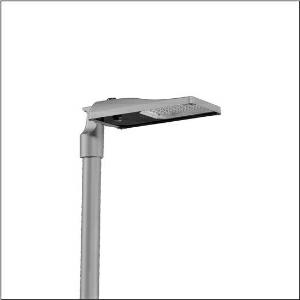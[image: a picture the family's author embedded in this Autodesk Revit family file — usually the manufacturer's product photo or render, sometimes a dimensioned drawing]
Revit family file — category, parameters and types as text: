
# Revit family: streetlight_sl_31_mini___p0_5a_5xh6v31t08ha_7d31
name_source: partatom
category: Lighting Fixtures
units: mm (PartAtom-declared; Revit-internal decimal feet)

## family parameters
Cut with Voids When Loaded = No
Host = Face
Light Source = No
Part Type = Normal
Room Calculation Point = No
Round Connector Dimension = Use Diameter
Shared = No

## types (1)
- --- (1 x LED, 9070 lm, 68.3 W, 3000K)
    Apparent Load = 68 VA
    CIE Flux Codes = 37 73 96 100 100
    Color Rendering = 70
    Color Temperature = 3000K
    Default Elevation = 1800 mm
    Description = Streetlight SL 31 mini D4i, Desk-Remote mast luminaire for post-top, side-entry; light control with lens of PMMA; light distribution: P0.5a, direct asymmetric distribution, for standard-compliant lighting for roads and squares; LED: luminous flux: 9.070lm, light colour: 730, colour temperature: 3000K; luminous efficacy: 132,8lm/W; control: pre-setting: logarithmic dimming characteristic, flexible luminous flux parameterisation, time-dependent luminous flux control, constant luminous flux control, power reduction, intelligent temperature release in ECG and LED module, overheat protection; luminaire housing, of diecast aluminium, SITECO metallic grey (DB 702S), corrosivity category C5 high according to DIN EN ISO 12944; cover of toughened safety glass, transparent, opened without tools; mast flange of diecast aluminium, SITECO metallic grey (DB 702S), spigot size: 76/60mm, mast flange included unmounted; cable length: 8,5m, connection cable pre-assembled; mains connection: 220..240V, AC, 50/60Hz; power consumption (at start of service life): 68,3W / (at end of service life): 74,5W / (with reduced operation 50%): 29,5W; protection rating (complete): IP66; insulation class (complete): insulation class II (safety insulation); impact resistance: IK09; certification: CE, ENEC, ENEC+, VDE, UKCA, ZD4i; permissible operating ambient temperature for outdoor applications: -40..+50°C; packaging unit: 1 piece

Light Distribution: P0.5a
    Height = 76 mm
    Lamp = 1 x LED
    Lamp Light Flux = 9070 lm
    Lamp Power = 68.3 W
    Lamp count = 1
    Length = 547 mm
    Luminous efficacy = 133 lm/W
    Manufacturer = Siteco
    ModVariant = No
    Model = 5XH6V31T08HA
    Number of Poles = 1
    OnlyDefault = Yes
    Power Factor = 1
    Product Name = Streetlight SL 31 mini | P0.5a
    Product group = mast luminaire | pylon top
    ProductGroupID = 6100
    Protection Class = Protection class II
    Protection Degree = IP 66
    RLX_Detail_Level = 1
    RLX_Emergency_Light_Flux = 0 lm
    RLX_Emergency_Type = 0
    RLX_Emergency_Type_DB = No
    RlxData = <blob elided: 23857 chars, md5=942e2b7b>
    Socket = socket
    Standby Power = 0 W
    System Light Flux = 9070 lm
    System Power = 68 W
    Type Comments = factory setting: luminous flux: 100 % | dim-lin: 254 | 692 mA
    Type Image = l_1300332.jpg
    URL = http://relux.com
    VarID = @adj_027489
    Voltage = 0 V
    Weight = 0.00 kg
    Width = 265 mm

## geometry (parser evidence)
native form markers: Blend x4, Sweep x12
no freeform markers — native parametric forms only
